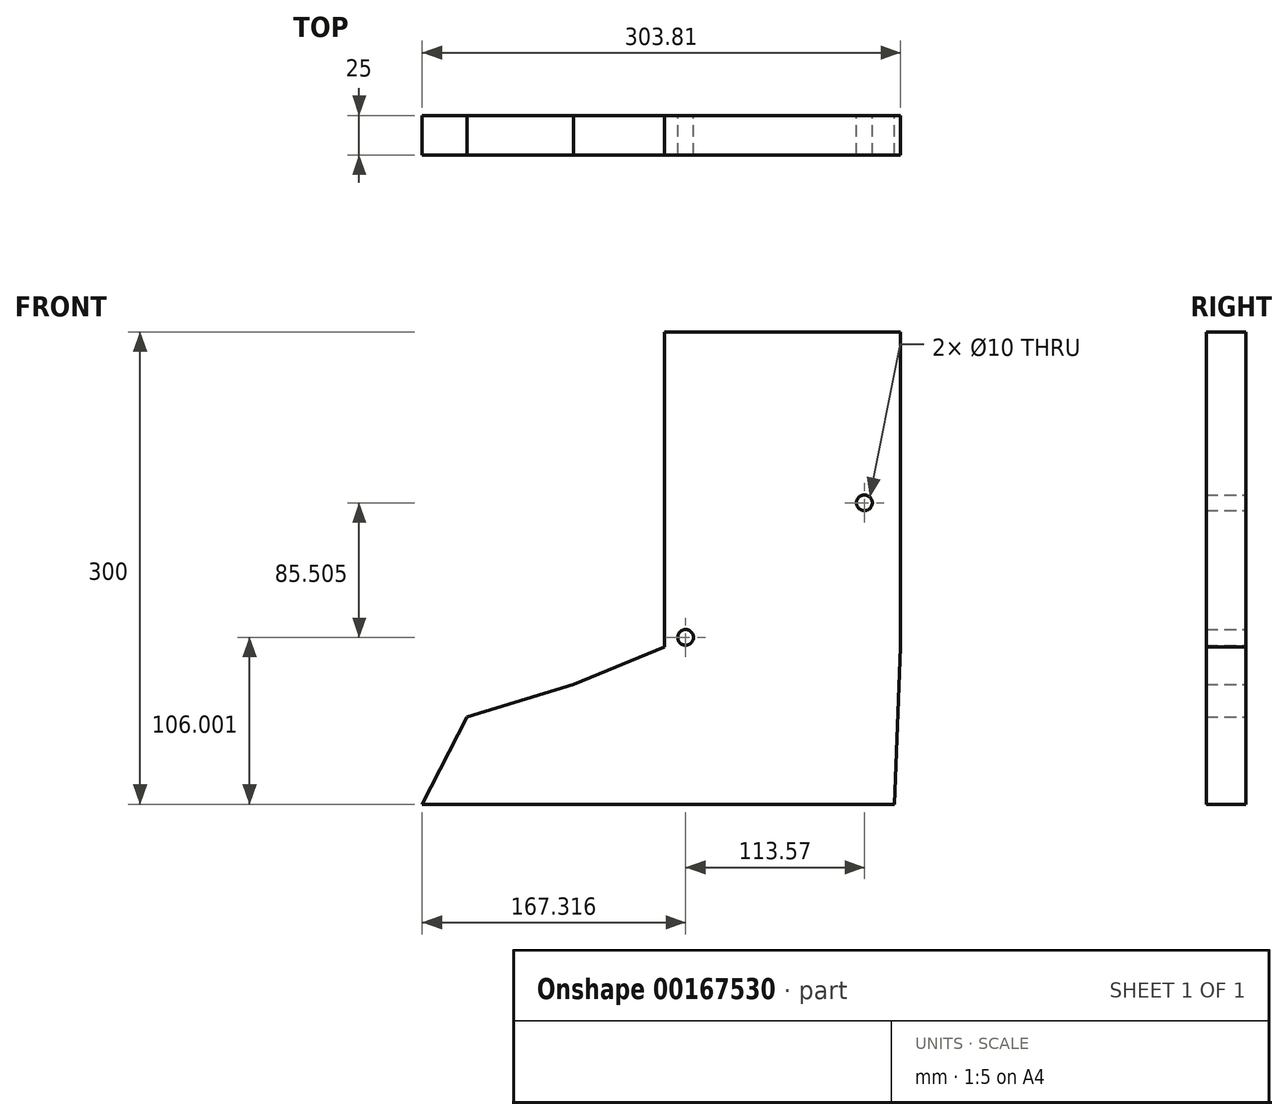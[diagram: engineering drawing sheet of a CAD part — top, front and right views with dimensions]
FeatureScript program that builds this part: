
annotation { "Feature Type Name" : "Feature", "Feature Type Description" : "" }
export const myFeature = defineFeature(function(context is Context, id is Id, definition is map)
    precondition{}
    {
        {
            var Q0;
            Q0=qCreatedBy(makeId("Front.planeOp"),FACE);
            var sketch = newSketch(context, id + "F0", { "sketchPlane" : qUnion([Q0])});
            skLineSegment(sketch, "E0.bottom", {"start": v(-100.85, 164.89) * mm, "end": v(49.15, 164.89) * mm});
            skLineSegment(sketch, "E0.top", {"start": v(-100.85, -35.11) * mm, "end": v(49.15, -35.11) * mm});
            skLineSegment(sketch, "E0.left", {"start": v(-100.85, 164.89) * mm, "end": v(-100.85, -35.11) * mm});
            skLineSegment(sketch, "E0.right", {"start": v(49.15, 164.89) * mm, "end": v(49.15, -35.11) * mm});
            skCircle(sketch, "E1", {"center": v(-87.34, -29.1) * mm, "radius": 5 * mm});
            skCircle(sketch, "E2", {"center": v(26.23, 56.4) * mm, "radius": 5 * mm});
            skLineSegment(sketch, "E3", {"start": v(-100.85, -35.11) * mm, "end": v(-158.59, -58.98) * mm});
            skLineSegment(sketch, "E4", {"start": v(-158.59, -58.98) * mm, "end": v(-226.02, -79.65) * mm});
            skLineSegment(sketch, "E5", {"start": v(-226.02, -79.65) * mm, "end": v(-254.66, -135.11) * mm});
            skLineSegment(sketch, "E6", {"start": v(-254.66, -135.11) * mm, "end": v(45.34, -135.11) * mm});
            skLineSegment(sketch, "E7", {"start": v(45.34, -135.11) * mm, "end": v(49.15, -35.11) * mm});
            skSolve(sketch);
        }
        {
            var Q0;
            Q0=makeQuery(id+"F0.imprint","IMPRINT",FACE,{"disambiguationData":[TD([[makeQuery(id+"F0.imprint","IMPRINT",EDGE,{"derivedFrom":sQuery(id+"F0.wireOp",EDGE,"E0.bottom")}),-1.0]])]});
            var Q1;
            Q1=makeQuery(id+"F0.imprint","IMPRINT",FACE,{"disambiguationData":[TD([[makeQuery(id+"F0.imprint","IMPRINT",EDGE,{"derivedFrom":sQuery(id+"F0.wireOp",EDGE,"E0.top")}),-1.0]])]});
            extrude(context, id + "F1", {"entities" : qUnion([Q0, Q1]), "depth" : 25 * mm});
        }
    });
